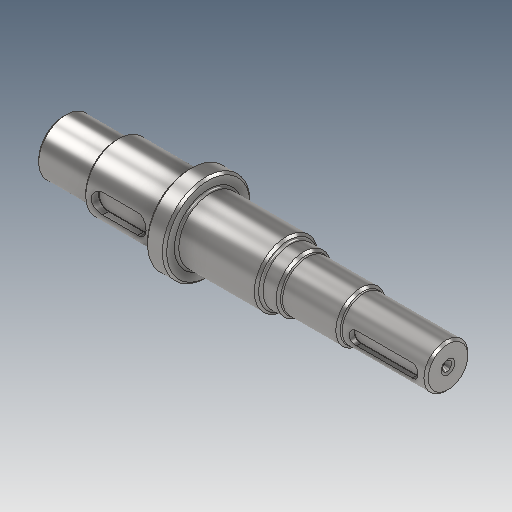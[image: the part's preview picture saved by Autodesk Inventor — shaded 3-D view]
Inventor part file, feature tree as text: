
AUTODESK INVENTOR PART (.ipt)
format: ipt  version: 2025 (Build 290162000, 162)  size: 345,600 bytes
history: native  units: mm
features: chamfer x8, other x7, revolve x2, fillet x1, sketch x1
ambient origin geometry x6: Origin, XZ Plane, XY Plane, X Axis, Y Axis, Z Axis
bodies: 实体1 (feature_tree)
feature tree (19):
  other  "{BB8FE430-83BF-418D-8DF9-9B323D3DB9B9}"
  revolve  "旋转1"  [1 undecoded]
  chamfer  "倒角10"  Distance=60.0mm
  chamfer  "倒角11"  Distance=80.0mm
  chamfer  "倒角12"  Distance=58.0mm
  chamfer  "倒角13"  Distance=50.0mm
  chamfer  "倒角14"  Distance=45.0mm
  chamfer  "倒角15"  Distance=40.0mm
  chamfer  "倒角16"  [1 undecoded]
  chamfer  "倒角17"  Distance=2.0mm
  other  "键槽2"
  other  "键槽3"
  fillet  "圆角1"  [1 undecoded]
  revolve  "旋转2"  Angle=120.0deg
  other  "起始平面"
  other  "主草图"
  other  "轴键槽"
  other  "轴键槽2"
  sketch  "草图3"  dims[d0=0.0mm d1=0.0mm d2=0.0mm d3=50.0mm d4=60.0mm d5=80.0mm d6=58.0mm d7=50.0mm d8=45.0mm d9=40.0mm d10=0.0mm d38=2.0mm d39=150.0deg d40=120.0deg d42=6.25mm d43=4.25mm d44=2.0mm d45=5.0mm d46=60.0deg d47=360.0deg d48=2.0mm d49=0.125mm d50=45.0deg d51=2.0mm d52=0.125mm d53=45.0deg d54=2.0mm d55=0.125mm d56=45.0deg d57=2.0mm d58=0.125mm d59=45.0deg d60=2.0mm d61=0.125mm d62=45.0deg d63=2.0mm d64=0.125mm d65=45.0deg d66=2.0mm d67=0.125mm d68=45.0deg d69=2.0mm d70=0.125mm d71=45.0deg d72=6.25mm d73=30.0deg d74=150.0deg d75=2.0mm d76=4.25mm d77=5.0mm d78=60.0deg]
note: 3 required parameter values undecoded (feature->parameter linkage not recoverable at this tier; creation-order binding heuristic only, values carry confidence <= 0.55)